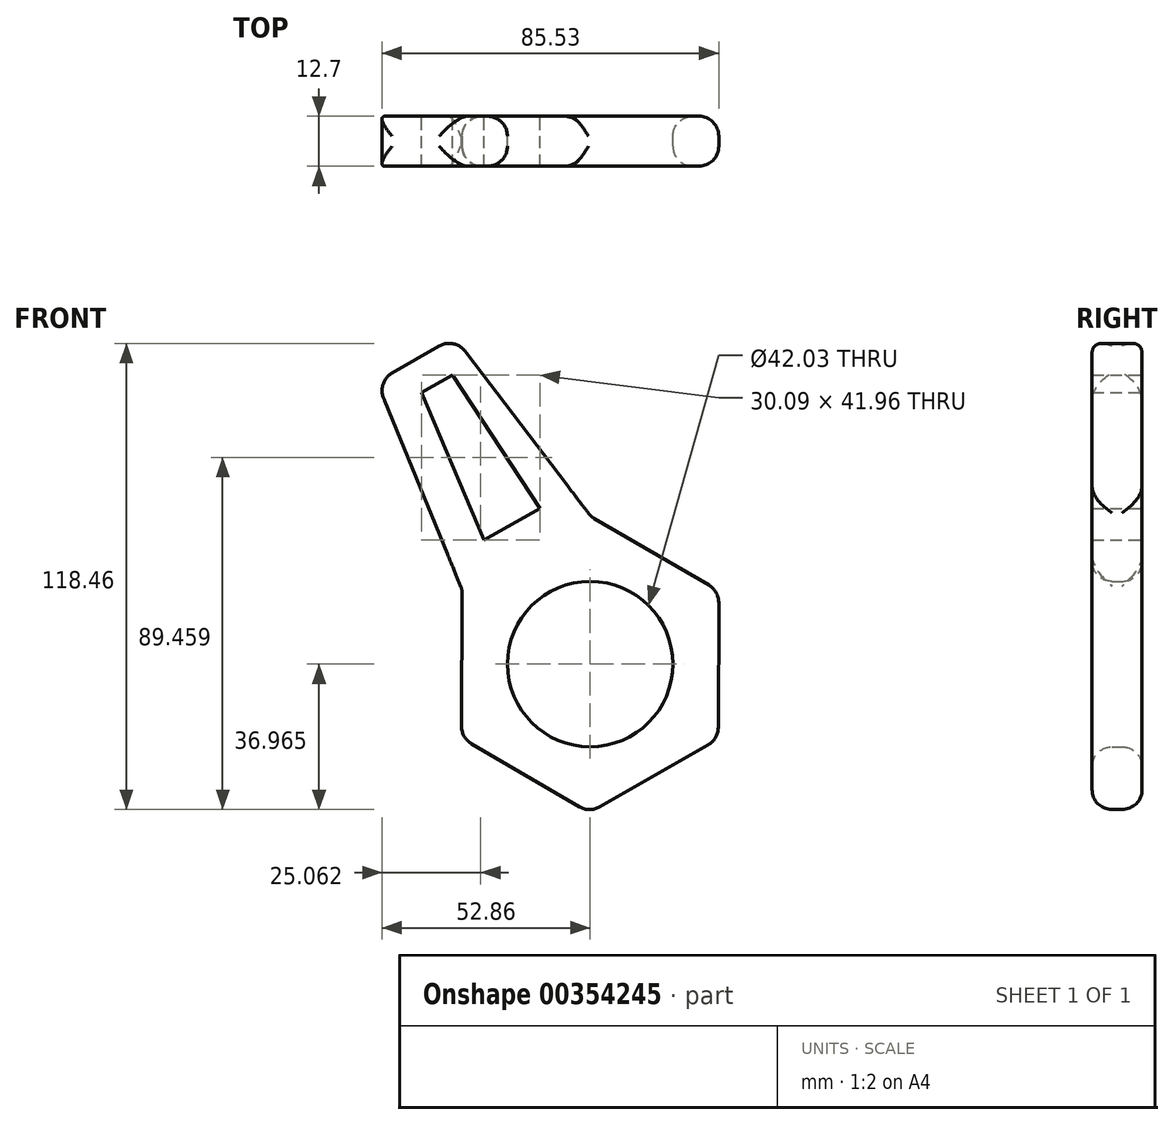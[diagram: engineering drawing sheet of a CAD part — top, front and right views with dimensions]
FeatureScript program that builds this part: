
annotation { "Feature Type Name" : "Feature", "Feature Type Description" : "" }
export const myFeature = defineFeature(function(context is Context, id is Id, definition is map)
    precondition{}
    {
        {
            var Q0;
            Q0=qCreatedBy(makeId("Front.planeOp"),FACE);
            var sketch = newSketch(context, id + "F0", { "sketchPlane" : qUnion([Q0])});
            skLineSegment(sketch, "E0.MirrorCS", {"start": v(-30.08, -32.6) * mm, "end": v(-29.92, 5.03) * mm});
            skLineSegment(sketch, "E1.MirrorCS", {"start": v(2.75, 23.72) * mm, "end": v(35.28, 4.77) * mm});
            skLineSegment(sketch, "E2.MirrorCS", {"start": v(35.28, 4.77) * mm, "end": v(35.12, -32.87) * mm});
            skLineSegment(sketch, "E3.MirrorCS", {"start": v(35.12, -32.87) * mm, "end": v(2.45, -51.56) * mm});
            skCircle(sketch, "E4.MirrorC", {"center": v(2.6, -13.92) * mm, "radius": 32.6 * mm, "construction": true});
            skLineSegment(sketch, "E5.MirrorCS", {"start": v(2.45, -51.56) * mm, "end": v(-30.08, -32.6) * mm});
            skPoint(sketch, "E6.MirrorP", {"position": v(-13.58, 14.38) * mm});
            skLineSegment(sketch, "E7.MirrorCS", {"start": v(-29.92, 5.03) * mm, "end": v(2.75, 23.72) * mm});
            skLineSegment(sketch, "E8.MirrorCS", {"start": v(2.75, 23.72) * mm, "end": v(-31.9, 69.24) * mm});
            skLineSegment(sketch, "E9.MirrorCS", {"start": v(-29.92, 5.03) * mm, "end": v(-51.57, 57.9) * mm});
            skLineSegment(sketch, "E10", {"start": v(-51.57, 57.9) * mm, "end": v(-31.9, 69.24) * mm});
            skCircle(sketch, "E11", {"center": v(2.6, -13.81) * mm, "radius": 21.01 * mm});
            skLineSegment(sketch, "E12", {"start": v(-10.16, 25.73) * mm, "end": v(-24.36, 17.7) * mm});
            skLineSegment(sketch, "E13", {"start": v(-24.36, 17.7) * mm, "end": v(-40.25, 55.23) * mm});
            skLineSegment(sketch, "E14", {"start": v(-40.25, 55.23) * mm, "end": v(-32.42, 59.66) * mm});
            skLineSegment(sketch, "E15", {"start": v(-32.42, 59.66) * mm, "end": v(-10.16, 25.73) * mm});
            skSolve(sketch);
        }
        {
            var Q0;
            Q0=makeQuery(id+"F0.imprint","IMPRINT",FACE,{"disambiguationData":[TD([[makeQuery(id+"F0.imprint","IMPRINT",EDGE,{"derivedFrom":sQuery(id+"F0.wireOp",EDGE,"E7.MirrorCS")}),1.0]])]});
            var Q1;
            Q1=makeQuery(id+"F0.imprint","IMPRINT",FACE,{"disambiguationData":[TD([[makeQuery(id+"F0.imprint","IMPRINT",EDGE,{"derivedFrom":sQuery(id+"F0.wireOp",EDGE,"E0.MirrorCS")}),-1.0]])]});
            extrude(context, id + "F1", {"entities" : qUnion([Q0, Q1]), "depth" : 12.7 * mm});
        }
        {
            var Q0;
            Q0=makeQuery(id+"F1.opExtrude","CAP_EDGE",EDGE,{"disambiguationData":[OSD([sQuery(id+"F0.wireOp",EDGE,"E11")])],"isStart":false});
            var Q1;
            Q1=makeQuery(id+"F1.opExtrude","SWEPT_FACE",FACE,{"disambiguationData":[OSD([sQuery(id+"F0.wireOp",EDGE,"E0.MirrorCS")])]});
            var Q2;
            Q2=makeQuery(id+"F1.opExtrude","SWEPT_FACE",FACE,{"disambiguationData":[OSD([sQuery(id+"F0.wireOp",EDGE,"E5.MirrorCS")])]});
            var Q3;
            Q3=makeQuery(id+"F1.opExtrude","SWEPT_FACE",FACE,{"disambiguationData":[OSD([sQuery(id+"F0.wireOp",EDGE,"E3.MirrorCS")])]});
            var Q4;
            Q4=makeQuery(id+"F1.opExtrude","SWEPT_FACE",FACE,{"disambiguationData":[OSD([sQuery(id+"F0.wireOp",EDGE,"E2.MirrorCS")])]});
            var Q5;
            Q5=makeQuery(id+"F1.opExtrude","SWEPT_FACE",FACE,{"disambiguationData":[OSD([sQuery(id+"F0.wireOp",EDGE,"E1.MirrorCS")])]});
            var Q6;
            Q6=makeQuery(id+"F1.opExtrude","SWEPT_FACE",FACE,{"disambiguationData":[OSD([sQuery(id+"F0.wireOp",EDGE,"E10")])]});
            var Q7;
            Q7=makeQuery(id+"F1.opExtrude","CAP_EDGE",EDGE,{"disambiguationData":[OSD([sQuery(id+"F0.wireOp",EDGE,"E11")])],"isStart":true});
            fillet(context, id + "F2", {"entities" : qUnion([Q0, Q1, Q2, Q3, Q4, Q5, Q6, Q7]), "radius" : 5.08 * mm, "tangentPropagation" : true, "allowEdgeOverflow" : false});
        }
    });
